# Revit family: Speaker-NearField-Panasonic-Wall_Mounted_RAMSA_WS-NF015_055_075SeriesX
name_source: partatom
category: Communication Devices
units: mm (PartAtom-declared; Revit-internal decimal feet)

## family parameters
Cut with Voids When Loaded = No
Host = Face
Maintain Annotation Orientation = Yes
OmniClass Number = 23.85.10.11.14.14.14
OmniClass Title = Loudspeakers
Part Type = Normal
Room Calculation Point = No
Round Connector Dimension = Use Diameter
Shared = No

## types (6) — shared parameters
Bracket Thickness = 3 mm  [stored 0.00984252 ft]
Bracket Width = 48 mm  [stored 0.15748 ft]
Date Last Modified = 2020/02/03
Default Elevation = 2700 mm  [stored 8.85827 ft]
Equipment Abbreviation = SP
Family Version = 1.0.0
Input connector = コネクター式端子台（4極）
Manufacturer = Panasonic
Model Disclaimer = Contact Panasonic for more information
Operational Temperature = -10℃~+50℃
Pan Handle Length = 100 mm  [stored 0.328084 ft]
Product Documentation Link = https://solcms.panasonic.biz
Product Page URL = https://sol.panasonic.biz
SV Visible = No
Type = 2ウェイバスレフ形
URL = https://biz.panasonic.com
View Volume Material = Panasonic - ViewVolume

## per-type parameters (varying)
- WS-NF015-W: Axis Distance from the Wall=86 mm  [stored 0.282152 ft]; Bracket Depth=86 mm  [stored 0.282152 ft]; Bracket Height=225 mm  [stored 0.738189 ft]; Coverage=130° x 130°; Depth=149 mm  [stored 0.488845 ft]; Description=RAMSA ニアフィールドスピーカー（屋内用）WS-NF015-W; Finish=エンクロージャー ：HIPS樹脂成型、白色（マンセルN9.3近似色）, パンチングネット ：金属製（SECC）、白色塗装（マンセルN9.3近似色）; Frequency characteristic=80 Hz～20 kHz（－20 dB）; Height=225 mm  [stored 0.738189 ft]; Input Impedance=ハイインピーダンス：100系、70系 330 Ω、670 Ω、1.3 kΩ, ローインピーダンス：8 Ω; Model=RAMSA ニアフィールドスピーカー（屋内用）WS-NF015-W; PHV=30; Pan Max Angle=80.00°; Pan Min Angle=-80.00°; Part Description=RAMSA ニアフィールドスピーカー（屋内用）WS-NF015-W; Power Handling=60 W（連続プログラム） / 30 W（RMS）; Product Material=Plastic - HIPS White (Munsell N9.3 Approx color）; Rated Input=100系 ：30 W、15 W、7.5 W, 70系 ：15 W、7.5 W、3.7 W; SPL=86 dB（1 m / 1 W）; Sound Coverage Horizontal Angle=130.00°; Sound Coverage Vertical Angle=130.00°; Sound Power Level=86; Speaker Front Offset=92 mm  [stored 0.301837 ft]; Speaker Type=15; Speaker unit=低域用 ：10 ㎝コーンウーハー, 高域用 ：2.5 ㎝ドームツィーター; Weight=2.50 kgf; Width=167 mm  [stored 0.5479 ft]
- WS-NF055-W: Axis Distance from the Wall=120 mm  [stored 0.393701 ft]; Bracket Depth=120 mm  [stored 0.393701 ft]; Bracket Height=297 mm  [stored 0.974409 ft]; Coverage=120°×65°; Depth=196 mm  [stored 0.643045 ft]; Description=RAMSA ニアフィールドスピーカー（屋内用）WS-NF055-W; Finish=エンクロージャー ：HIPS樹脂成型、白色（マンセルN9.3近似色）, パンチングネット ：金属製（SECC）、白色塗装（マンセルN9.3近似色）; Frequency characteristic=60 Hz～20 kHz（－20 dB）; Height=300 mm; Input Impedance=ハイインピーダンス：100系、70系 167 Ω、330 Ω、670 Ω, ローインピーダンス：8 Ω; Model=RAMSA ニアフィールドスピーカー（屋内用）WS-NF055-W; PHV=60; Pan Max Angle=80.00°; Pan Min Angle=-80.00°; Part Description=RAMSA ニアフィールドスピーカー（屋内用）WS-NF055-W; Power Handling=120 W（連続プログラム） / 60 W（RMS）; Product Material=Plastic - HIPS White (Munsell N9.3 Approx color）; Rated Input=100系 ：60 W、30 W、15 W, 70系 ：30 W、15 W、7.5 W; SPL=88 dB（1 m / 1 W）; Sound Coverage Horizontal Angle=120.00°; Sound Coverage Vertical Angle=65.00°; Sound Power Level=88; Speaker Front Offset=112 mm  [stored 0.367454 ft]; Speaker Type=55; Speaker unit=低域用 ：16 ㎝コーンウーハー, 高域用 ：2.5 ㎝ドームツィーター; Weight=3.80 kgf; Width=230 mm  [stored 0.754593 ft]
- WS-NF075-W: Axis Distance from the Wall=141 mm; Bracket Depth=141 mm; Bracket Height=361 mm  [stored 1.18438 ft]; Coverage=80°×40°; Depth=219 mm  [stored 0.718504 ft]; Description=RAMSA ニアフィールドスピーカー（屋内用）WS-NF075-W; Finish=エンクロージャー ：HIPS樹脂成型、白色（マンセルN9.3近似色）, パンチングネット ：金属製（SECC）、白色塗装（マンセルN9.3近似色）; Frequency characteristic=55 Hz～20 kHz（－20 dB）; Height=380 mm; Input Impedance=ハイインピーダンス：100系、70系 126 Ω、167 Ω、330 Ω, ローインピーダンス：8 Ω; Model=RAMSA ニアフィールドスピーカー（屋内用）WS-NF075-W; PHV=90; Pan Max Angle=40.00°; Pan Min Angle=-40.00°; Part Description=RAMSA ニアフィールドスピーカー（屋内用）WS-NF075-W; Power Handling=180 W（連続プログラム） / 90 W（RMS）; Product Material=Plastic - HIPS White (Munsell N9.3 Approx color）; Rated Input=100系 ：80 W、60 W、30 W, 70系 ：40 W、30 W、15 W; SPL=90 dB（1 m / 1 W）; Sound Coverage Horizontal Angle=80.00°; Sound Coverage Vertical Angle=40.00°; Sound Power Level=90; Speaker Front Offset=135 mm  [stored 0.442913 ft]; Speaker Type=75; Speaker unit=低域用 ：20 ㎝コーンウーハー, 高域用 ：2.5 ㎝ドームツィーター; Weight=5.70 kgf; Width=278 mm  [stored 0.912073 ft]
- WS-NF015-K: Axis Distance from the Wall=86 mm  [stored 0.282152 ft]; Bracket Depth=86 mm  [stored 0.282152 ft]; Bracket Height=225 mm  [stored 0.738189 ft]; Coverage=130° x 130°; Depth=149 mm  [stored 0.488845 ft]; Description=RAMSA ニアフィールドスピーカー（屋内用）WS-NF015-K; Finish=エンクロージャー ：HIPS樹脂成型、黒色（マンセルN1近似色）, パンチングネット ：金属製（SECC）、黒色塗装（マンセルN1近似色）; Frequency characteristic=80 Hz～20 kHz（－20 dB）; Height=225 mm  [stored 0.738189 ft]; Input Impedance=ハイインピーダンス：100系、70系 330 Ω、670 Ω、1.3 kΩ, ローインピーダンス：8 Ω; Model=RAMSA ニアフィールドスピーカー（屋内用）WS-NF015-K; PHV=30; Pan Max Angle=80.00°; Pan Min Angle=-80.00°; Part Description=RAMSA ニアフィールドスピーカー（屋内用）WS-NF015-K; Power Handling=60 W（連続プログラム） / 30 W（RMS）; Product Material=Plastic - HIPS Black (Munsell N1 Approx color); Rated Input=100系 ：30 W、15 W、7.5 W, 70系 ：15 W、7.5 W、3.7 W; SPL=86 dB（1 m / 1 W）; Sound Coverage Horizontal Angle=130.00°; Sound Coverage Vertical Angle=130.00°; Sound Power Level=86; Speaker Front Offset=92 mm  [stored 0.301837 ft]; Speaker Type=15; Speaker unit=低域用 ：10 ㎝コーンウーハー, 高域用 ：2.5 ㎝ドームツィーター; Weight=2.50 kgf; Width=167 mm  [stored 0.5479 ft]
- WS-NF055-K: Axis Distance from the Wall=120 mm  [stored 0.393701 ft]; Bracket Depth=120 mm  [stored 0.393701 ft]; Bracket Height=297 mm  [stored 0.974409 ft]; Coverage=120°×65°; Depth=196 mm  [stored 0.643045 ft]; Description=RAMSA ニアフィールドスピーカー（屋内用）WS-NF055-K; Finish=エンクロージャー ：HIPS樹脂成型、黒色（マンセルN1近似色）, パンチングネット ：金属製（SECC）、黒色塗装（マンセルN1近似色）; Frequency characteristic=60 Hz～20 kHz（－20 dB）; Height=300 mm; Input Impedance=ハイインピーダンス：100系、70系 167 Ω、330 Ω、670 Ω, ローインピーダンス：8 Ω; Model=RAMSA ニアフィールドスピーカー（屋内用）WS-NF055-K; PHV=60; Pan Max Angle=80.00°; Pan Min Angle=-80.00°; Part Description=RAMSA ニアフィールドスピーカー（屋内用）WS-NF055-K; Power Handling=120 W（連続プログラム） / 60 W（RMS）; Product Material=Plastic - HIPS Black (Munsell N1 Approx color); Rated Input=100系 ：60 W、30 W、15 W, 70系 ：30 W、15 W、7.5 W; SPL=88 dB（1 m / 1 W）; Sound Coverage Horizontal Angle=120.00°; Sound Coverage Vertical Angle=65.00°; Sound Power Level=88; Speaker Front Offset=112 mm  [stored 0.367454 ft]; Speaker Type=55; Speaker unit=低域用 ：16 ㎝コーンウーハー, 高域用 ：2.5 ㎝ドームツィーター; Weight=3.80 kgf; Width=230 mm  [stored 0.754593 ft]
- WS-NF075-K: Axis Distance from the Wall=141 mm; Bracket Depth=141 mm; Bracket Height=361 mm  [stored 1.18438 ft]; Coverage=80°×40°; Depth=219 mm  [stored 0.718504 ft]; Description=RAMSA ニアフィールドスピーカー（屋内用）WS-NF075-K; Finish=エンクロージャー ：HIPS樹脂成型、黒色（マンセルN1近似色）, パンチングネット ：金属製（SECC）、黒色塗装（マンセルN1近似色）; Frequency characteristic=55 Hz～20 kHz（－20 dB）; Height=380 mm; Input Impedance=ハイインピーダンス：100系、70系 126 Ω、167 Ω、330 Ω, ローインピーダンス：8 Ω; Model=RAMSA ニアフィールドスピーカー（屋内用）WS-NF075-K; PHV=90; Pan Max Angle=40.00°; Pan Min Angle=-40.00°; Part Description=RAMSA ニアフィールドスピーカー（屋内用）WS-NF075-K; Power Handling=180 W（連続プログラム） / 90 W（RMS）; Product Material=Plastic - HIPS Black (Munsell N1 Approx color); Rated Input=100系 ：80 W、60 W、30 W, 70系 ：40 W、30 W、15 W; SPL=90 dB（1 m / 1 W）; Sound Coverage Horizontal Angle=80.00°; Sound Coverage Vertical Angle=40.00°; Sound Power Level=90; Speaker Front Offset=135 mm  [stored 0.442913 ft]; Speaker Type=75; Speaker unit=低域用 ：20 ㎝コーンウーハー, 高域用 ：2.5 ㎝ドームツィーター; Weight=5.70 kgf; Width=278 mm  [stored 0.912073 ft]

note: column(s) folded — value = type name in every type: Part Number

note: [stored X ft] marks values corroborated as IEEE doubles in the binary element streams (Revit-internal decimal feet)

## geometry (parser evidence)
native form markers: Sweep x6
no freeform markers — native parametric forms only
